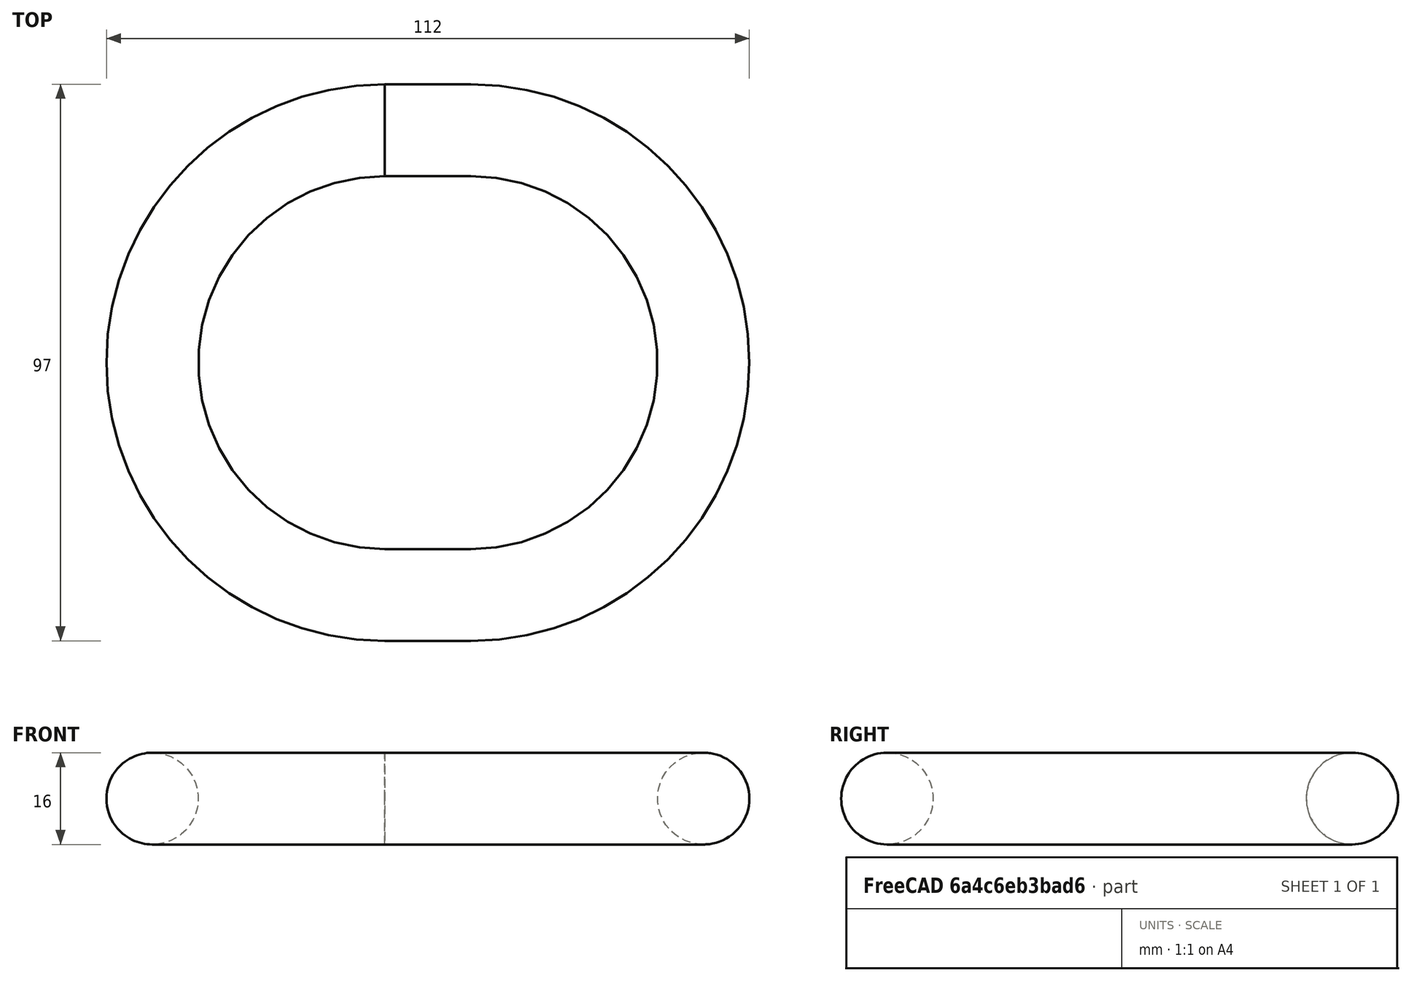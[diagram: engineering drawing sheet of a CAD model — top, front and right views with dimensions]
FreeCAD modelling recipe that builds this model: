
FCSTD DOCUMENT  (FreeCAD 0.17R11586 (Git))
Label: hook
License: All rights reserved
LicenseURL: http://en.wikipedia.org/wiki/All_rights_reserved
objects: Sketcher::SketchObject×2, PartDesign::Plane×1, PartDesign::AdditivePipe×1, PartDesign::Body×1
note: 6 computed .brp shape members not serialized (recipe doc carries the construction recipe); baked Part::Feature solids carry a one-line shape summary decoded from their .brp

FEATURE [Sketcher::SketchObject] Sketch
  MapMode = 5
  Support = -> [XY_Plane]
  sketch-geometry (4):
    g0: ArcOfCircle CenterX=-7.5 CenterY=0 CenterZ=0 NormalX=0 NormalY=0 NormalZ=1 Radius=40.5 StartAngle=1.5708 EndAngle=4.71239
    g1: ArcOfCircle CenterX=7.5 CenterY=0 CenterZ=0 NormalX=0 NormalY=0 NormalZ=1 Radius=40.5 StartAngle=4.71239 EndAngle=7.85398
    g2: LineSegment StartX=-7.50008 StartY=40.5 StartZ=0 EndX=7.5 EndY=40.5 EndZ=0
    g3: LineSegment StartX=-7.50008 StartY=-40.5 StartZ=0 EndX=7.5 EndY=-40.5 EndZ=0
  constraints (14):
    c: Equal(g0,g1)
    c: PointOnObject(g0,g-1)
    c: PointOnObject(g1,g-1)
    c: Coincident(g2,g0)
    c: Coincident(g2,g1)
    c: Horizontal(g2)
    c: Coincident(g3,g0)
    c: Coincident(g3,g1)
    c: Horizontal(g3)
    c: Radius(g0) = 40.5
    c: Tangent(g3,g0)
    c: Tangent(g0,g2)
    c: Symmetric(g0,g1,g-2)
    c: DistanceX(g0,g-1) = 7.5
FEATURE [PartDesign::Plane] DatumPlane
  MapMode = 8
  Placement = pos=(-7.50008,40.5,0) rot=(0.57735,0.577351,0.577351;2.0944rad)
  Support = -> [Sketch]
FEATURE [Sketcher::SketchObject] Sketch001
  MapMode = 5
  Placement = pos=(-7.50008,40.5,0) rot=(0.57735,0.577351,0.577351;2.0944rad)
  Support = -> [DatumPlane]
  sketch-geometry (1):
    g0: Circle CenterX=0 CenterY=0 CenterZ=0 NormalX=0 NormalY=0 NormalZ=1 Radius=8
  constraints (2):
    c: Coincident(g0,g-1)
    c: Radius(g0) = 8
FEATURE [PartDesign::AdditivePipe] AdditivePipe
  AuxilleryCurvelinear = true
  AuxillerySpineTangent = false
  Binormal = (0,0,0)
  Mode = 0
  Placement = pos=(-7.50008,40.5,0) rot=(0.57735,0.577351,0.577351;2.0944rad)
  Profile = -> Sketch001
  Spine = -> Sketch
  SpineTangent = false
  Transformation = 0
  Transition = 0
FEATURE [PartDesign::Body] Body
  Group = -> [Sketch,DatumPlane,Sketch001,AdditivePipe]
  Origin = -> Origin
  Tip = -> AdditivePipe
